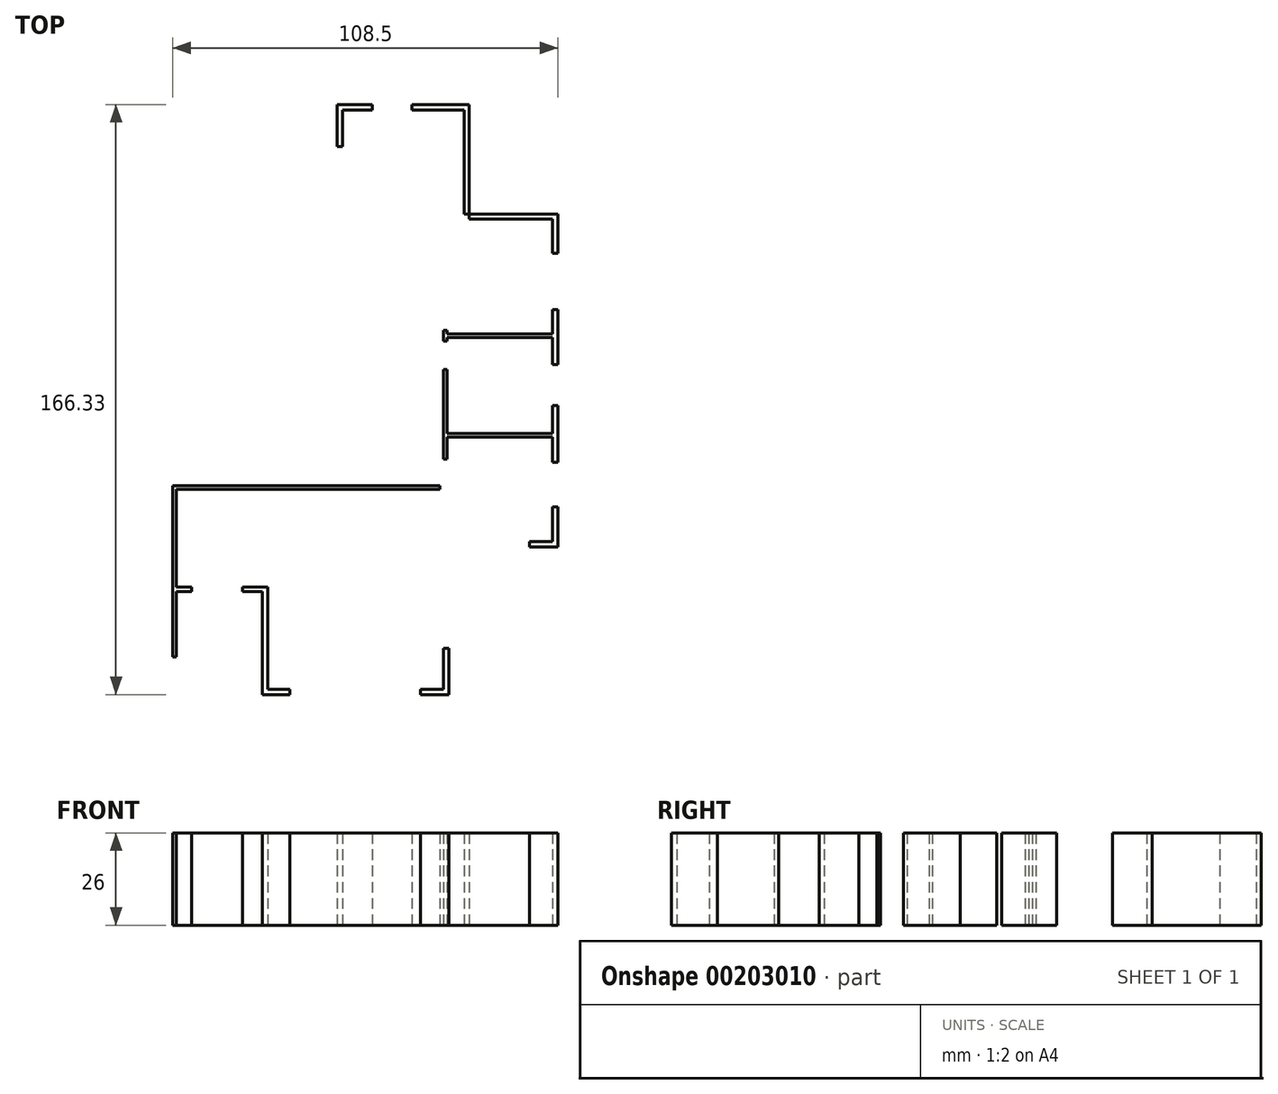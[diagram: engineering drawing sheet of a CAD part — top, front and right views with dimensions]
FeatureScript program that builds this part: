
annotation { "Feature Type Name" : "Feature", "Feature Type Description" : "" }
export const myFeature = defineFeature(function(context is Context, id is Id, definition is map)
    precondition{}
    {
        {
            var Q0;
            Q0=qCreatedBy(makeId("Top.planeOp"),FACE);
            var sketch = newSketch(context, id + "F0", { "sketchPlane" : qUnion([Q0])});
            skLineSegment(sketch, "E0.bottom", {"start": v(-9.97, 0) * mm, "end": v(-28.5, 0) * mm});
            skLineSegment(sketch, "E0.top", {"start": v(0, 38.84) * mm, "end": v(-28.5, 38.84) * mm});
            skLineSegment(sketch, "E0.left", {"start": v(0, 0) * mm, "end": v(0, 9.04) * mm});
            skLineSegment(sketch, "E0.right", {"start": v(-28.5, 0) * mm, "end": v(-28.5, 38.84) * mm});
            skLineSegment(sketch, "E1.bottom", {"start": v(-30, 40.34) * mm, "end": v(0, 40.34) * mm});
            skLineSegment(sketch, "E1.top", {"start": v(-28.5, 0) * mm, "end": v(-9.97, 0) * mm});
            skLineSegment(sketch, "E1.left", {"start": v(-30, 40.34) * mm, "end": v(-30, 0) * mm});
            skLineSegment(sketch, "E1.right", {"start": v(0, 9.04) * mm, "end": v(0, 0) * mm});
            skLineSegment(sketch, "E2.bottom", {"start": v(-30, 40.34) * mm, "end": v(-37.5, 40.34) * mm});
            skLineSegment(sketch, "E2.top", {"start": v(-30, 21.34) * mm, "end": v(-37.5, 21.34) * mm});
            skLineSegment(sketch, "E2.left", {"start": v(-30, 40.34) * mm, "end": v(-30, 21.34) * mm});
            skLineSegment(sketch, "E2.right", {"start": v(-37.5, 40.34) * mm, "end": v(-37.5, 21.34) * mm});
            skLineSegment(sketch, "E3.bottom", {"start": v(-30, 21.54) * mm, "end": v(-28.5, 21.54) * mm});
            skLineSegment(sketch, "E3.top", {"start": v(-30, 28.54) * mm, "end": v(-28.5, 28.54) * mm});
            skLineSegment(sketch, "E3.left", {"start": v(-30, 21.54) * mm, "end": v(-30, 28.54) * mm});
            skLineSegment(sketch, "E3.right", {"start": v(-28.5, 21.54) * mm, "end": v(-28.5, 28.54) * mm});
            skLineSegment(sketch, "E4.bottom", {"start": v(-20.12, 38.84) * mm, "end": v(-8.97, 38.84) * mm});
            skLineSegment(sketch, "E4.top", {"start": v(-20.12, 40.34) * mm, "end": v(-8.97, 40.34) * mm});
            skLineSegment(sketch, "E4.left", {"start": v(-20.12, 38.84) * mm, "end": v(-20.12, 40.34) * mm});
            skLineSegment(sketch, "E4.right", {"start": v(-8.97, 38.84) * mm, "end": v(-8.97, 40.34) * mm});
            skLineSegment(sketch, "E5.left", {"start": v(0, 0) * mm, "end": v(0, -10.09) * mm});
            skLineSegment(sketch, "E6.bottom", {"start": v(0, 38.84) * mm, "end": v(5.75, 38.84) * mm});
            skLineSegment(sketch, "E6.top", {"start": v(0, 9.04) * mm, "end": v(5.75, 9.04) * mm});
            skLineSegment(sketch, "E6.right", {"start": v(5.75, 38.84) * mm, "end": v(5.75, 9.04) * mm});
            skLineSegment(sketch, "E7", {"start": v(0, 40.34) * mm, "end": v(7.25, 40.34) * mm});
            skLineSegment(sketch, "E8", {"start": v(7.25, 40.34) * mm, "end": v(7.25, 4.25) * mm});
            skLineSegment(sketch, "E9.MirrorCS", {"start": v(0, -10.09) * mm, "end": v(-9.97, -10.09) * mm});
            skLineSegment(sketch, "E10.MirrorCS", {"start": v(-9.97, 0) * mm, "end": v(-9.97, -10.09) * mm});
            skLineSegment(sketch, "E11.bottom", {"start": v(1, 8.04) * mm, "end": v(30.7, 8.04) * mm});
            skLineSegment(sketch, "E11.top", {"start": v(1, -24.26) * mm, "end": v(30.7, -24.26) * mm});
            skLineSegment(sketch, "E11.left", {"start": v(1, 8.04) * mm, "end": v(1, -24.26) * mm});
            skLineSegment(sketch, "E11.right", {"start": v(30.7, 8.04) * mm, "end": v(30.7, -24.26) * mm});
            skLineSegment(sketch, "E12.bottom", {"start": v(5.75, 9.54) * mm, "end": v(32.2, 9.54) * mm});
            skLineSegment(sketch, "E12.top", {"start": v(5.75, -25.26) * mm, "end": v(30.7, -25.26) * mm});
            skLineSegment(sketch, "E12.left", {"start": v(5.75, 9.54) * mm, "end": v(5.75, 9.04) * mm});
            skLineSegment(sketch, "E12.right", {"start": v(32.2, 9.54) * mm, "end": v(32.2, -25.26) * mm});
            skLineSegment(sketch, "E13.bottom", {"start": v(-10.97, -1) * mm, "end": v(-28.17, -1) * mm});
            skLineSegment(sketch, "E13.top", {"start": v(-10.97, -21.6) * mm, "end": v(-28.17, -21.6) * mm});
            skLineSegment(sketch, "E13.left", {"start": v(-10.97, -1) * mm, "end": v(-10.97, -21.6) * mm});
            skLineSegment(sketch, "E14.bottom", {"start": v(-9.97, -11.09) * mm, "end": v(0, -11.09) * mm});
            skLineSegment(sketch, "E14.top", {"start": v(-9.97, -67.09) * mm, "end": v(0, -67.09) * mm});
            skLineSegment(sketch, "E14.left", {"start": v(-9.97, -11.09) * mm, "end": v(-9.97, -53.1) * mm});
            skLineSegment(sketch, "E14.right", {"start": v(0, -11.09) * mm, "end": v(0, -67.09) * mm});
            skLineSegment(sketch, "E15.bottom", {"start": v(-22.27, -22.6) * mm, "end": v(-10.97, -22.6) * mm});
            skLineSegment(sketch, "E15.top", {"start": v(-28.17, -48) * mm, "end": v(-10.97, -48) * mm});
            skLineSegment(sketch, "E15.right", {"start": v(-10.97, -22.6) * mm, "end": v(-10.97, -48) * mm});
            skLineSegment(sketch, "E16.bottom", {"start": v(-10.97, -1.94) * mm, "end": v(-9.97, -1.94) * mm});
            skLineSegment(sketch, "E16.top", {"start": v(-10.97, -8.94) * mm, "end": v(-9.97, -8.94) * mm});
            skLineSegment(sketch, "E16.left", {"start": v(-10.97, -1.94) * mm, "end": v(-10.97, -8.94) * mm});
            skLineSegment(sketch, "E16.right", {"start": v(-9.97, -1.94) * mm, "end": v(-9.97, -8.94) * mm});
            skLineSegment(sketch, "E17.bottom", {"start": v(-10.47, -1.94) * mm, "end": v(-17.47, -1.94) * mm});
            skLineSegment(sketch, "E17.top", {"start": v(-10.47, -2.44) * mm, "end": v(-17.47, -2.44) * mm});
            skLineSegment(sketch, "E17.left", {"start": v(-10.47, -1.94) * mm, "end": v(-10.47, -2.44) * mm});
            skLineSegment(sketch, "E17.right", {"start": v(-17.47, -1.94) * mm, "end": v(-17.47, -2.44) * mm});
            skLineSegment(sketch, "E18.bottom", {"start": v(-10.97, -22.6) * mm, "end": v(-22.27, -22.6) * mm});
            skLineSegment(sketch, "E18.left", {"start": v(-10.97, -22.6) * mm, "end": v(-10.97, -30.6) * mm});
            skLineSegment(sketch, "E18.right", {"start": v(-22.27, -22.6) * mm, "end": v(-22.27, -30.6) * mm});
            skLineSegment(sketch, "E19.bottom", {"start": v(-22.27, -30.6) * mm, "end": v(-27.87, -30.6) * mm});
            skLineSegment(sketch, "E19.left", {"start": v(-10.97, -30.6) * mm, "end": v(-10.97, -38.6) * mm});
            skLineSegment(sketch, "E19.right", {"start": v(-27.87, -30.6) * mm, "end": v(-27.87, -38.6) * mm});
            skLineSegment(sketch, "E20.top", {"start": v(-10.97, -48) * mm, "end": v(-28.17, -48) * mm});
            skLineSegment(sketch, "E20.left", {"start": v(-10.97, -38.6) * mm, "end": v(-10.97, -48) * mm});
            skLineSegment(sketch, "E21", {"start": v(-28.5, -1) * mm, "end": v(-28.5, -21.6) * mm});
            skLineSegment(sketch, "E22.bottom", {"start": v(-10.97, -1) * mm, "end": v(-28.5, -1) * mm});
            skLineSegment(sketch, "E22.top", {"start": v(-10.97, -21.6) * mm, "end": v(-28.5, -21.6) * mm});
            skLineSegment(sketch, "E23.left", {"start": v(-23.06, -22.6) * mm, "end": v(-23.06, -29.81) * mm});
            skLineSegment(sketch, "E24", {"start": v(-29.5, -1) * mm, "end": v(-29.5, -20.03) * mm});
            skLineSegment(sketch, "E25.bottom", {"start": v(-30, 0) * mm, "end": v(-29.5, 0) * mm});
            skLineSegment(sketch, "E25.top", {"start": v(-30, -1) * mm, "end": v(-29.5, -1) * mm});
            skLineSegment(sketch, "E25.left", {"start": v(-30, 0) * mm, "end": v(-30, -1) * mm});
            skLineSegment(sketch, "E26.top", {"start": v(-10.97, -48) * mm, "end": v(-28.5, -48) * mm});
            skLineSegment(sketch, "E26.right", {"start": v(-28.5, -22.6) * mm, "end": v(-28.5, -29.81) * mm});
            skLineSegment(sketch, "E27.bottom", {"start": v(-27.87, -38.6) * mm, "end": v(-28.5, -38.6) * mm});
            skLineSegment(sketch, "E27.left", {"start": v(-27.87, -38.6) * mm, "end": v(-27.87, -30.6) * mm});
            skLineSegment(sketch, "E27.right", {"start": v(-28.5, -38.6) * mm, "end": v(-28.5, -30.6) * mm});
            skLineSegment(sketch, "E28.bottom", {"start": v(-28.5, -22.6) * mm, "end": v(-23.06, -22.6) * mm});
            skLineSegment(sketch, "E28.top", {"start": v(-28.5, -29.81) * mm, "end": v(-23.06, -29.81) * mm});
            skLineSegment(sketch, "E29.trimOffspring", {"start": v(-28.5, -30.6) * mm, "end": v(-28.5, -48) * mm});
            skLineSegment(sketch, "E30", {"start": v(-29.5, -20.03) * mm, "end": v(-29.5, -42.93) * mm});
            skLineSegment(sketch, "E31.bottom", {"start": v(1, -25.26) * mm, "end": v(30.7, -25.26) * mm});
            skLineSegment(sketch, "E31.top", {"start": v(1, -52.36) * mm, "end": v(30.7, -52.36) * mm});
            skLineSegment(sketch, "E31.left", {"start": v(1, -25.26) * mm, "end": v(1, -52.36) * mm});
            skLineSegment(sketch, "E31.right", {"start": v(30.7, -25.26) * mm, "end": v(30.7, -52.36) * mm});
            skLineSegment(sketch, "E32.bottom", {"start": v(1, -53.36) * mm, "end": v(30.7, -53.36) * mm});
            skLineSegment(sketch, "E32.top", {"start": v(1, -82.86) * mm, "end": v(30.7, -82.86) * mm});
            skLineSegment(sketch, "E32.left", {"start": v(1, -53.36) * mm, "end": v(1, -82.86) * mm});
            skLineSegment(sketch, "E32.right", {"start": v(30.7, -53.36) * mm, "end": v(30.7, -82.86) * mm});
            skLineSegment(sketch, "E33.top", {"start": v(1.5, -84.36) * mm, "end": v(32.2, -84.36) * mm});
            skLineSegment(sketch, "E33.left", {"start": v(1, -25.26) * mm, "end": v(1, -82.86) * mm});
            skLineSegment(sketch, "E33.right", {"start": v(32.2, -25.26) * mm, "end": v(32.2, -84.36) * mm});
            skLineSegment(sketch, "E34.bottom", {"start": v(-29.47, -49.5) * mm, "end": v(-10.97, -49.5) * mm});
            skLineSegment(sketch, "E34.top", {"start": v(-29.47, -67.09) * mm, "end": v(-10.97, -67.09) * mm});
            skLineSegment(sketch, "E34.left", {"start": v(-29.47, -49.5) * mm, "end": v(-29.47, -67.09) * mm});
            skLineSegment(sketch, "E34.right", {"start": v(-10.97, -49.5) * mm, "end": v(-10.97, -53.1) * mm});
            skLineSegment(sketch, "E35.bottom", {"start": v(0, -68.09) * mm, "end": v(-49.6, -68.09) * mm});
            skLineSegment(sketch, "E35.top", {"start": v(0, -124.49) * mm, "end": v(-49.6, -124.49) * mm});
            skLineSegment(sketch, "E35.left", {"start": v(0, -68.09) * mm, "end": v(0, -124.49) * mm});
            skLineSegment(sketch, "E35.right", {"start": v(-49.6, -95.69) * mm, "end": v(-49.6, -124.49) * mm});
            skLineSegment(sketch, "E36.bottom", {"start": v(-49.6, -68.09) * mm, "end": v(-75.3, -68.09) * mm});
            skLineSegment(sketch, "E36.top", {"start": v(-56.6, -115.29) * mm, "end": v(-75.3, -115.29) * mm});
            skLineSegment(sketch, "E36.right", {"start": v(-75.3, -68.09) * mm, "end": v(-75.3, -95.69) * mm});
            skLineSegment(sketch, "E37.top", {"start": v(1.5, -125.99) * mm, "end": v(-51.1, -125.99) * mm});
            skLineSegment(sketch, "E37.left", {"start": v(1.5, -84.36) * mm, "end": v(1.5, -125.99) * mm});
            skLineSegment(sketch, "E37.right", {"start": v(-51.1, -97) * mm, "end": v(-51.1, -125.99) * mm});
            skLineSegment(sketch, "E38.trimOffspring", {"start": v(-49.6, -95.69) * mm, "end": v(-51.1, -95.69) * mm});
            skLineSegment(sketch, "E39.bottom", {"start": v(-51.1, -97) * mm, "end": v(-75.3, -97) * mm});
            skLineSegment(sketch, "E39.top", {"start": v(-51.1, -115.29) * mm, "end": v(-75.3, -115.29) * mm});
            skLineSegment(sketch, "E39.left", {"start": v(-51.1, -97) * mm, "end": v(-51.1, -115.29) * mm});
            skLineSegment(sketch, "E39.right", {"start": v(-75.3, -97) * mm, "end": v(-75.3, -115.29) * mm});
            skLineSegment(sketch, "E40.bottom", {"start": v(-51.1, -95.69) * mm, "end": v(-75.3, -95.69) * mm});
            skLineSegment(sketch, "E40.top", {"start": v(-51.1, -68.09) * mm, "end": v(-75.3, -68.09) * mm});
            skLineSegment(sketch, "E40.right", {"start": v(-75.3, -95.69) * mm, "end": v(-75.3, -68.09) * mm});
            skLineSegment(sketch, "E41.bottom", {"start": v(-29.47, -67.09) * mm, "end": v(-76.3, -67.09) * mm});
            skLineSegment(sketch, "E41.right", {"start": v(-76.3, -67.09) * mm, "end": v(-76.3, -115.29) * mm});
            skLineSegment(sketch, "E42.trimOffspring", {"start": v(-51.1, -115.29) * mm, "end": v(-76.3, -115.29) * mm});
            skLineSegment(sketch, "E43.bottom", {"start": v(-43.33, -124.49) * mm, "end": v(-6.55, -124.49) * mm});
            skLineSegment(sketch, "E43.top", {"start": v(-43.33, -125.99) * mm, "end": v(-6.55, -125.99) * mm});
            skLineSegment(sketch, "E43.left", {"start": v(-43.33, -124.49) * mm, "end": v(-43.33, -125.99) * mm});
            skLineSegment(sketch, "E43.right", {"start": v(-6.55, -124.49) * mm, "end": v(-6.55, -125.99) * mm});
            skLineSegment(sketch, "E44.bottom", {"start": v(0, -93.55) * mm, "end": v(1.5, -93.55) * mm});
            skLineSegment(sketch, "E44.top", {"start": v(0, -112.97) * mm, "end": v(1.5, -112.97) * mm});
            skLineSegment(sketch, "E44.left", {"start": v(0, -93.55) * mm, "end": v(0, -112.97) * mm});
            skLineSegment(sketch, "E44.right", {"start": v(1.5, -93.55) * mm, "end": v(1.5, -112.97) * mm});
            skLineSegment(sketch, "E45.bottom", {"start": v(9.55, -82.86) * mm, "end": v(24.23, -82.86) * mm});
            skLineSegment(sketch, "E45.top", {"start": v(9.55, -84.36) * mm, "end": v(24.23, -84.36) * mm});
            skLineSegment(sketch, "E45.left", {"start": v(9.55, -82.86) * mm, "end": v(9.55, -84.36) * mm});
            skLineSegment(sketch, "E45.right", {"start": v(24.23, -82.86) * mm, "end": v(24.23, -84.36) * mm});
            skLineSegment(sketch, "E46.bottom", {"start": v(-71, -95.69) * mm, "end": v(-56.65, -95.69) * mm});
            skLineSegment(sketch, "E46.top", {"start": v(-71, -97) * mm, "end": v(-56.65, -97) * mm});
            skLineSegment(sketch, "E46.left", {"start": v(-71, -95.69) * mm, "end": v(-71, -97) * mm});
            skLineSegment(sketch, "E46.right", {"start": v(-56.65, -95.69) * mm, "end": v(-56.65, -97) * mm});
            skLineSegment(sketch, "E47.bottom", {"start": v(30.7, -60.54) * mm, "end": v(32.2, -60.54) * mm});
            skLineSegment(sketch, "E47.top", {"start": v(30.7, -73.08) * mm, "end": v(32.2, -73.08) * mm});
            skLineSegment(sketch, "E47.left", {"start": v(30.7, -60.54) * mm, "end": v(30.7, -73.08) * mm});
            skLineSegment(sketch, "E47.right", {"start": v(32.2, -60.54) * mm, "end": v(32.2, -73.08) * mm});
            skLineSegment(sketch, "E48.bottom", {"start": v(30.7, -32.9) * mm, "end": v(32.2, -32.9) * mm});
            skLineSegment(sketch, "E48.top", {"start": v(30.7, -44.51) * mm, "end": v(32.2, -44.51) * mm});
            skLineSegment(sketch, "E48.left", {"start": v(30.7, -32.9) * mm, "end": v(30.7, -44.51) * mm});
            skLineSegment(sketch, "E48.right", {"start": v(32.2, -32.9) * mm, "end": v(32.2, -44.51) * mm});
            skLineSegment(sketch, "E49.bottom", {"start": v(30.7, -1.6) * mm, "end": v(32.2, -1.6) * mm});
            skLineSegment(sketch, "E49.top", {"start": v(30.7, -17.37) * mm, "end": v(32.2, -17.37) * mm});
            skLineSegment(sketch, "E49.left", {"start": v(30.7, -1.6) * mm, "end": v(30.7, -17.37) * mm});
            skLineSegment(sketch, "E49.right", {"start": v(32.2, -1.6) * mm, "end": v(32.2, -17.37) * mm});
            skLineSegment(sketch, "E50.bottom", {"start": v(-10.97, -49.5) * mm, "end": v(-29.47, -49.5) * mm});
            skLineSegment(sketch, "E50.top", {"start": v(-10.97, -53.1) * mm, "end": v(-29.47, -53.1) * mm});
            skLineSegment(sketch, "E51.bottom", {"start": v(-29.47, -67.09) * mm, "end": v(-30.97, -67.09) * mm});
            skLineSegment(sketch, "E51.top", {"start": v(-29.47, -42.93) * mm, "end": v(-30.97, -42.93) * mm});
            skLineSegment(sketch, "E51.left", {"start": v(-29.47, -53.1) * mm, "end": v(-29.47, -49.5) * mm});
            skLineSegment(sketch, "E51.right", {"start": v(-30.97, -67.09) * mm, "end": v(-30.97, -42.93) * mm});
            skPoint(sketch, "E52.orphan", {"position": v(-29.5, -49.5) * mm});
            skPoint(sketch, "E53.orphan", {"position": v(-28.5, -49.5) * mm});
            skLineSegment(sketch, "E54", {"start": v(-10.97, -53.1) * mm, "end": v(-9.97, -53.1) * mm});
            skLineSegment(sketch, "E55.bottom", {"start": v(-10.97, -67.09) * mm, "end": v(-9.97, -67.09) * mm});
            skLineSegment(sketch, "E55.top", {"start": v(-10.97, -68.09) * mm, "end": v(-9.97, -68.09) * mm});
            skLineSegment(sketch, "E56.bottom", {"start": v(-10, -67.09) * mm, "end": v(-1, -67.09) * mm});
            skLineSegment(sketch, "E56.top", {"start": v(-10, -68.09) * mm, "end": v(-1, -68.09) * mm});
            skLineSegment(sketch, "E56.left", {"start": v(-10, -67.09) * mm, "end": v(-10, -68.09) * mm});
            skLineSegment(sketch, "E56.right", {"start": v(-1, -67.09) * mm, "end": v(-1, -68.09) * mm});
            skLineSegment(sketch, "E57.bottom", {"start": v(-1, -67.59) * mm, "end": v(-1.05, -67.59) * mm});
            skLineSegment(sketch, "E57.top", {"start": v(-1, -76.59) * mm, "end": v(-1.05, -76.59) * mm});
            skLineSegment(sketch, "E57.left", {"start": v(-1, -67.59) * mm, "end": v(-1, -76.59) * mm});
            skLineSegment(sketch, "E57.right", {"start": v(-1.05, -67.59) * mm, "end": v(-1.05, -76.59) * mm});
            skLineSegment(sketch, "E58.bottom", {"start": v(0, -66.59) * mm, "end": v(1, -66.59) * mm});
            skLineSegment(sketch, "E58.top", {"start": v(0, -59.59) * mm, "end": v(1, -59.59) * mm});
            skLineSegment(sketch, "E58.left", {"start": v(0, -66.59) * mm, "end": v(0, -59.59) * mm});
            skLineSegment(sketch, "E58.right", {"start": v(1, -66.59) * mm, "end": v(1, -59.59) * mm});
            skLineSegment(sketch, "E59.bottom", {"start": v(0, -26.26) * mm, "end": v(1, -26.26) * mm});
            skLineSegment(sketch, "E59.top", {"start": v(0, -34.26) * mm, "end": v(1, -34.26) * mm});
            skLineSegment(sketch, "E59.left", {"start": v(0, -26.26) * mm, "end": v(0, -34.26) * mm});
            skLineSegment(sketch, "E59.right", {"start": v(1, -26.26) * mm, "end": v(1, -34.26) * mm});
            skLineSegment(sketch, "E60.bottom", {"start": v(0.5, -26.26) * mm, "end": v(8.5, -26.26) * mm});
            skLineSegment(sketch, "E60.top", {"start": v(0.5, -26.76) * mm, "end": v(8.5, -26.76) * mm});
            skLineSegment(sketch, "E60.left", {"start": v(0.5, -26.26) * mm, "end": v(0.5, -26.76) * mm});
            skLineSegment(sketch, "E60.right", {"start": v(8.5, -26.26) * mm, "end": v(8.5, -26.76) * mm});
            skLineSegment(sketch, "E61.bottom", {"start": v(0, -23.26) * mm, "end": v(1, -23.26) * mm});
            skLineSegment(sketch, "E61.top", {"start": v(0, -15.26) * mm, "end": v(1, -15.26) * mm});
            skLineSegment(sketch, "E61.left", {"start": v(0, -23.26) * mm, "end": v(0, -15.26) * mm});
            skLineSegment(sketch, "E61.right", {"start": v(1, -23.26) * mm, "end": v(1, -15.26) * mm});
            skLineSegment(sketch, "E62.bottom", {"start": v(0.5, -23.26) * mm, "end": v(8.5, -23.26) * mm});
            skLineSegment(sketch, "E62.top", {"start": v(0.5, -22.76) * mm, "end": v(8.5, -22.76) * mm});
            skLineSegment(sketch, "E62.left", {"start": v(0.5, -23.26) * mm, "end": v(0.5, -22.76) * mm});
            skLineSegment(sketch, "E62.right", {"start": v(8.5, -23.26) * mm, "end": v(8.5, -22.76) * mm});
            skPoint(sketch, "E63.MirrorCS.start.orphan", {"position": v(0, 0) * mm});
            skLineSegment(sketch, "E64.bottom", {"start": v(-8.97, -10.09) * mm, "end": v(-0.97, -10.09) * mm});
            skLineSegment(sketch, "E64.top", {"start": v(-8.97, -11.09) * mm, "end": v(-0.97, -11.09) * mm});
            skLineSegment(sketch, "E64.left", {"start": v(-8.97, -10.09) * mm, "end": v(-8.97, -11.09) * mm});
            skLineSegment(sketch, "E64.right", {"start": v(-0.97, -10.09) * mm, "end": v(-0.97, -11.09) * mm});
            skLineSegment(sketch, "E65.bottom", {"start": v(-0.97, -10.59) * mm, "end": v(-1.47, -10.59) * mm});
            skLineSegment(sketch, "E65.top", {"start": v(-0.97, -2.59) * mm, "end": v(-1.47, -2.59) * mm});
            skLineSegment(sketch, "E65.left", {"start": v(-0.97, -10.59) * mm, "end": v(-0.97, -2.59) * mm});
            skLineSegment(sketch, "E65.right", {"start": v(-1.47, -10.59) * mm, "end": v(-1.47, -2.59) * mm});
            skLineSegment(sketch, "E66.bottom", {"start": v(-29.25, 21.54) * mm, "end": v(-22.25, 21.54) * mm});
            skLineSegment(sketch, "E66.top", {"start": v(-29.25, 21.94) * mm, "end": v(-22.25, 21.94) * mm});
            skLineSegment(sketch, "E66.left", {"start": v(-29.25, 21.54) * mm, "end": v(-29.25, 21.94) * mm});
            skLineSegment(sketch, "E66.right", {"start": v(-22.25, 21.54) * mm, "end": v(-22.25, 21.94) * mm});
            skSolve(sketch);
        }
        {
            var Q0;
            {var subQ3=sQuery(id+"F0.wireOp",EDGE,"E3.top");Q0=makeQuery(id+"F0.imprint","IMPRINT",FACE,{"disambiguationData":[TD([[makeQuery(id+"F0.imprint","IMPRINT",EDGE,{"derivedFrom":subQ3}),1.0]])]});}
            var Q1;
            {var subQ1=sQuery(id+"F0.wireOp",EDGE,"E4.right");Q1=makeQuery(id+"F0.imprint","IMPRINT",FACE,{"disambiguationData":[TD([[makeQuery(id+"F0.imprint","IMPRINT",EDGE,{"derivedFrom":subQ1}),-1.0]])]});}
            var Q2;
            {var subQ3=sQuery(id+"F0.wireOp",EDGE,"E49.bottom");Q2=makeQuery(id+"F0.imprint","IMPRINT",FACE,{"disambiguationData":[TD([[makeQuery(id+"F0.imprint","IMPRINT",EDGE,{"derivedFrom":subQ3}),1.0]])]});}
            var Q3;
            Q3=makeQuery(id+"F0.imprint","IMPRINT",FACE,{"disambiguationData":[TD([[makeQuery(id+"F0.imprint","IMPRINT",EDGE,{"derivedFrom":sQuery(id+"F0.wireOp",EDGE,"E1.right")}),1.0]])]});
            var Q4;
            {var subQ19=sQuery(id+"F0.wireOp",EDGE,"E1.top");Q4=makeQuery(id+"F0.imprint","IMPRINT",FACE,{"disambiguationData":[TD([[makeQuery(id+"F0.imprint","IMPRINT",EDGE,{"derivedFrom":subQ19}),-1.0]])]});}
            var Q5;
            {var subQ3=sQuery(id+"F0.wireOp",EDGE,"E31.top");Q5=makeQuery(id+"F0.imprint","IMPRINT",FACE,{"disambiguationData":[TD([[makeQuery(id+"F0.imprint","IMPRINT",EDGE,{"derivedFrom":subQ3}),-1.0]])]});}
            var Q6;
            {var subQ7=sQuery(id+"F0.wireOp",EDGE,"E45.right");Q6=makeQuery(id+"F0.imprint","IMPRINT",FACE,{"disambiguationData":[TD([[makeQuery(id+"F0.imprint","IMPRINT",EDGE,{"derivedFrom":subQ7}),1.0]])]});}
            var Q7;
            {var subQ13=sQuery(id+"F0.wireOp",EDGE,"E14.top");Q7=makeQuery(id+"F0.imprint","IMPRINT",FACE,{"disambiguationData":[TD([[makeQuery(id+"F0.imprint","IMPRINT",EDGE,{"derivedFrom":subQ13}),-1.0]])]});}
            var Q8;
            {var subQ4=sQuery(id+"F0.wireOp",EDGE,"E43.right");Q8=makeQuery(id+"F0.imprint","IMPRINT",FACE,{"disambiguationData":[TD([[makeQuery(id+"F0.imprint","IMPRINT",EDGE,{"derivedFrom":subQ4}),1.0]])]});}
            var Q9;
            {var subQ5=sQuery(id+"F0.wireOp",EDGE,"E35.right");Q9=makeQuery(id+"F0.imprint","IMPRINT",FACE,{"disambiguationData":[TD([[makeQuery(id+"F0.imprint","IMPRINT",EDGE,{"derivedFrom":subQ5}),-1.0]])]});}
            var Q10;
            Q10=makeQuery(id+"F0.imprint","IMPRINT",FACE,{"disambiguationData":[TD([[makeQuery(id+"F0.imprint","IMPRINT",EDGE,{"derivedFrom":sQuery(id+"F0.wireOp",EDGE,"E34.top")}),-1.0]])]});
            var Q11;
            {var subQ18=sQuery(id+"F0.wireOp",EDGE,"E11.top");Q11=makeQuery(id+"F0.imprint","IMPRINT",FACE,{"disambiguationData":[TD([[makeQuery(id+"F0.imprint","IMPRINT",EDGE,{"derivedFrom":subQ18}),-1.0]])]});}
            var Q12;
            {var subQ2=sQuery(id+"F0.wireOp",EDGE,"E58.top");Q12=makeQuery(id+"F0.imprint","IMPRINT",FACE,{"disambiguationData":[TD([[makeQuery(id+"F0.imprint","IMPRINT",EDGE,{"derivedFrom":subQ2}),1.0]])]});}
            extrude(context, id + "F1", {"entities" : qUnion([Q0, Q1, Q2, Q3, Q4, Q5, Q6, Q7, Q8, Q9, Q10, Q11, Q12]), "depth" : 26 * mm});
        }
    });
